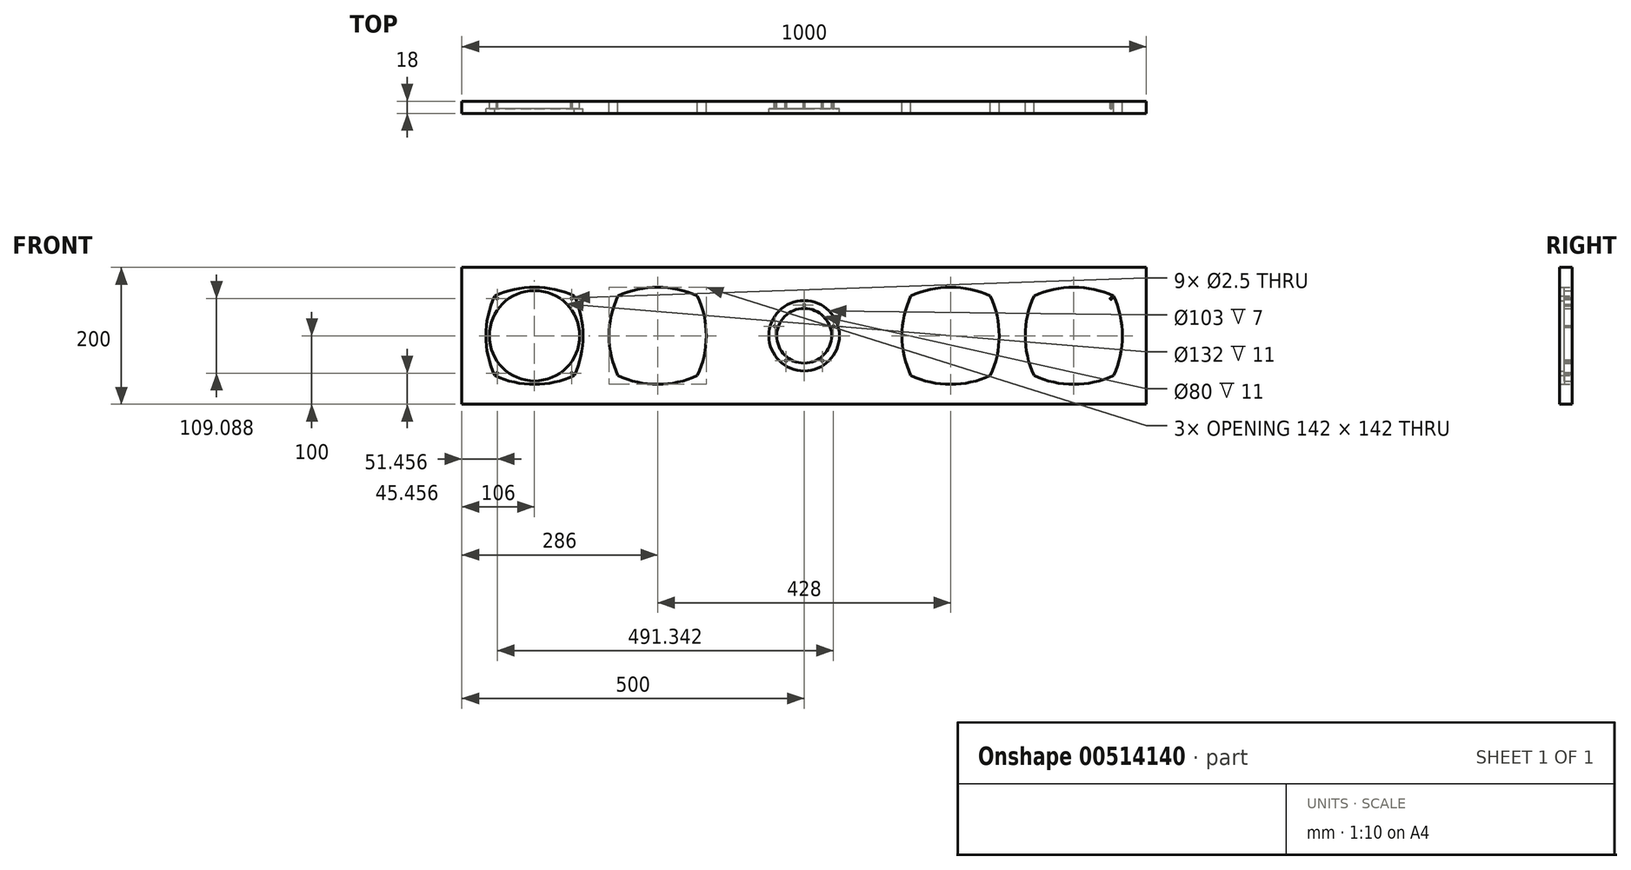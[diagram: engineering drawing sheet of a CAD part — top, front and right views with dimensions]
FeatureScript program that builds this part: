
annotation { "Feature Type Name" : "Feature", "Feature Type Description" : "" }
export const myFeature = defineFeature(function(context is Context, id is Id, definition is map)
    precondition{}
    {
        {
            var Q0;
            Q0=qCreatedBy(makeId("Front.planeOp"),FACE);
            var sketch = newSketch(context, id + "F0", { "sketchPlane" : qUnion([Q0])});
            skLineSegment(sketch, "E0.bottom", {"start": v(500, 100) * mm, "end": v(-500, 100) * mm});
            skLineSegment(sketch, "E0.top", {"start": v(500, -100) * mm, "end": v(-500, -100) * mm});
            skLineSegment(sketch, "E0.left", {"start": v(500, 100) * mm, "end": v(500, -100) * mm});
            skLineSegment(sketch, "E0.right", {"start": v(-500, 100) * mm, "end": v(-500, -100) * mm});
            skPoint(sketch, "E0.middle", {"position": v(0, 0) * mm});
            skCircle(sketch, "E1", {"center": v(-394, 0) * mm, "radius": 66 * mm});
            skCircle(sketch, "E2", {"center": v(0, 0) * mm, "radius": 40 * mm});
            skCircle(sketch, "E3", {"center": v(0, 0) * mm, "radius": 45 * mm});
            skCircle(sketch, "E4", {"center": v(0, 0) * mm, "radius": 51.5 * mm});
            skCircle(sketch, "E5", {"center": v(0, 45) * mm, "radius": 1.25 * mm});
            skCircle(sketch, "E6.1.0", {"center": v(-42.8, 13.9) * mm, "radius": 1.25 * mm});
            skCircle(sketch, "E6.2.0", {"center": v(-26.45, -36.4) * mm, "radius": 1.25 * mm});
            skCircle(sketch, "E6.3.0", {"center": v(26.45, -36.4) * mm, "radius": 1.25 * mm});
            skCircle(sketch, "E6.4.0", {"center": v(42.8, 13.9) * mm, "radius": 1.25 * mm});
            skArc(sketch, "E7", {"start": v(-335.92, 58.08) * mm, "mid": v(-394, 71) * mm, "end": v(-452.08, 58.08) * mm});
            skArc(sketch, "E8", {"start": v(-452.08, 58.08) * mm, "mid": v(-465, 0) * mm, "end": v(-452.08, -58.08) * mm});
            skArc(sketch, "E9", {"start": v(-452.08, -58.08) * mm, "mid": v(-394, -71) * mm, "end": v(-335.92, -58.08) * mm});
            skArc(sketch, "E10", {"start": v(-335.92, -58.08) * mm, "mid": v(-323, 0) * mm, "end": v(-335.92, 58.08) * mm});
            skLineSegment(sketch, "E11", {"start": v(-452.08, 58.08) * mm, "end": v(-335.92, -58.08) * mm, "construction": true});
            skLineSegment(sketch, "E12", {"start": v(-335.92, 58.08) * mm, "end": v(-452.08, -58.08) * mm, "construction": true});
            skCircle(sketch, "E13", {"center": v(-448.54, 54.54) * mm, "radius": 1.25 * mm});
            skCircle(sketch, "E14.1.0", {"center": v(-448.54, -54.54) * mm, "radius": 1.25 * mm});
            skCircle(sketch, "E14.2.0", {"center": v(-339.46, -54.54) * mm, "radius": 1.25 * mm});
            skCircle(sketch, "E14.3.0", {"center": v(-339.46, 54.54) * mm, "radius": 1.25 * mm});
            skCircle(sketch, "E15.MirrorC", {"center": v(448.54, 54.54) * mm, "radius": 1.25 * mm});
            skCircle(sketch, "E16.MirrorC", {"center": v(339.46, -54.54) * mm, "radius": 1.25 * mm});
            skCircle(sketch, "E17.MirrorC", {"center": v(448.54, -54.54) * mm, "radius": 1.25 * mm});
            skCircle(sketch, "E18.MirrorC", {"center": v(339.46, 54.54) * mm, "radius": 1.25 * mm});
            skLineSegment(sketch, "E19.MirrorCS", {"start": v(335.92, 58.08) * mm, "end": v(452.08, -58.08) * mm, "construction": true});
            skLineSegment(sketch, "E20.MirrorCS", {"start": v(452.08, 58.08) * mm, "end": v(335.92, -58.08) * mm, "construction": true});
            skPoint(sketch, "E21.MirrorP", {"position": v(394, 0) * mm});
            skArc(sketch, "E22.MirrorCS", {"start": v(452.08, 58.08) * mm, "mid": v(465, 0) * mm, "end": v(452.08, -58.08) * mm});
            skArc(sketch, "E23.MirrorCS", {"start": v(452.08, -58.08) * mm, "mid": v(394, -71) * mm, "end": v(335.92, -58.08) * mm});
            skCircle(sketch, "E24.MirrorC", {"center": v(394, 0) * mm, "radius": 66 * mm});
            skArc(sketch, "E25.MirrorCS", {"start": v(335.92, -58.08) * mm, "mid": v(323, 0) * mm, "end": v(335.92, 58.08) * mm});
            skArc(sketch, "E26.MirrorCS", {"start": v(335.92, 58.08) * mm, "mid": v(394, 71) * mm, "end": v(452.08, 58.08) * mm});
            skCircle(sketch, "E27", {"center": v(-214, 0) * mm, "radius": 66 * mm});
            skArc(sketch, "E28", {"start": v(-155.92, 58.08) * mm, "mid": v(-214, 71) * mm, "end": v(-272.08, 58.08) * mm});
            skArc(sketch, "E29", {"start": v(-272.08, 58.08) * mm, "mid": v(-285, 0) * mm, "end": v(-272.08, -58.08) * mm});
            skArc(sketch, "E30", {"start": v(-272.08, -58.08) * mm, "mid": v(-214, -71) * mm, "end": v(-155.92, -58.08) * mm});
            skArc(sketch, "E31", {"start": v(-155.92, -58.08) * mm, "mid": v(-143, 0) * mm, "end": v(-155.92, 58.08) * mm});
            skLineSegment(sketch, "E32", {"start": v(-272.08, 58.08) * mm, "end": v(-155.92, -58.08) * mm, "construction": true});
            skLineSegment(sketch, "E33", {"start": v(-155.92, 58.08) * mm, "end": v(-272.08, -58.08) * mm, "construction": true});
            skCircle(sketch, "E34", {"center": v(-268.54, 54.54) * mm, "radius": 1.25 * mm});
            skCircle(sketch, "E35.1.0", {"center": v(-268.54, -54.54) * mm, "radius": 1.25 * mm});
            skCircle(sketch, "E35.2.0", {"center": v(-159.46, -54.54) * mm, "radius": 1.25 * mm});
            skCircle(sketch, "E35.3.0", {"center": v(-159.46, 54.54) * mm, "radius": 1.25 * mm});
            skCircle(sketch, "E36.MirrorC", {"center": v(268.54, 54.54) * mm, "radius": 1.25 * mm});
            skCircle(sketch, "E37.MirrorC", {"center": v(268.54, -54.54) * mm, "radius": 1.25 * mm});
            skCircle(sketch, "E38.MirrorC", {"center": v(159.46, -54.54) * mm, "radius": 1.25 * mm});
            skCircle(sketch, "E39.MirrorC", {"center": v(159.46, 54.54) * mm, "radius": 1.25 * mm});
            skArc(sketch, "E40.MirrorCS", {"start": v(155.92, 58.08) * mm, "mid": v(214, 71) * mm, "end": v(272.08, 58.08) * mm});
            skLineSegment(sketch, "E41.MirrorCS", {"start": v(272.08, 58.08) * mm, "end": v(155.92, -58.08) * mm, "construction": true});
            skLineSegment(sketch, "E42.MirrorCS", {"start": v(155.92, 58.08) * mm, "end": v(272.08, -58.08) * mm, "construction": true});
            skArc(sketch, "E43.MirrorCS", {"start": v(155.92, -58.08) * mm, "mid": v(143, 0) * mm, "end": v(155.92, 58.08) * mm});
            skArc(sketch, "E44.MirrorCS", {"start": v(272.08, -58.08) * mm, "mid": v(214, -71) * mm, "end": v(155.92, -58.08) * mm});
            skPoint(sketch, "E45.MirrorP", {"position": v(214, 0) * mm});
            skCircle(sketch, "E46.MirrorC", {"center": v(214, 0) * mm, "radius": 66 * mm});
            skArc(sketch, "E47.MirrorCS", {"start": v(272.08, 58.08) * mm, "mid": v(285, 0) * mm, "end": v(272.08, -58.08) * mm});
            skSolve(sketch);
        }
        {
            var Q0;
            {var subQ0=sQuery(id+"F0.wireOp",EDGE,"OdRPwVkJ-LgnD-wcSP-26Xd-tCm6PIhxOoPI.bottom");var subQ1=sQuery(id+"F0.wireOp",EDGE,"WheFQNC1-m6lz-ETYG-WdT4-gUt766dIlw9O");var subQ2=makeQuery(id+"F0.imprint","INTERSECT",VERTEX,{"disambiguationData":[OD(0.0)],"derivedFrom":[subQ1,subQ0]});Q0=makeQuery(id+"F0.imprint","IMPRINT",FACE,{"disambiguationData":[TD([[makeQuery(id+"F0.imprint","IMPRINT",EDGE,{"disambiguationData":[TD([[subQ2,-1.0]])],"derivedFrom":subQ1}),1.0]])]});}
            var Q1;
            {var subQ0=sQuery(id+"F0.wireOp",EDGE,"OdRPwVkJ-LgnD-wcSP-26Xd-tCm6PIhxOoPI.bottom");var subQ1=sQuery(id+"F0.wireOp",EDGE,"WheFQNC1-m6lz-ETYG-WdT4-gUt766dIlw9O");var subQ2=makeQuery(id+"F0.imprint","INTERSECT",VERTEX,{"disambiguationData":[OD(0.0)],"derivedFrom":[subQ1,subQ0]});Q1=makeQuery(id+"F0.imprint","IMPRINT",FACE,{"disambiguationData":[TD([[makeQuery(id+"F0.imprint","IMPRINT",EDGE,{"disambiguationData":[TD([[subQ2,1.0]])],"derivedFrom":subQ1}),-1.0]])]});}
            var Q2;
            {var subQ0=sQuery(id+"F0.wireOp",EDGE,"OdRPwVkJ-LgnD-wcSP-26Xd-tCm6PIhxOoPI.bottom");var subQ1=sQuery(id+"F0.wireOp",EDGE,"WheFQNC1-m6lz-ETYG-WdT4-gUt766dIlw9O");var subQ2=makeQuery(id+"F0.imprint","INTERSECT",VERTEX,{"disambiguationData":[OD(1.0)],"derivedFrom":[subQ1,subQ0]});Q2=makeQuery(id+"F0.imprint","IMPRINT",FACE,{"disambiguationData":[TD([[makeQuery(id+"F0.imprint","IMPRINT",EDGE,{"disambiguationData":[TD([[subQ2,-1.0]])],"derivedFrom":subQ1}),-1.0]])]});}
            var Q3;
            {var subQ0=sQuery(id+"F0.wireOp",EDGE,"OdRPwVkJ-LgnD-wcSP-26Xd-tCm6PIhxOoPI.right");var subQ1=sQuery(id+"F0.wireOp",EDGE,"WheFQNC1-m6lz-ETYG-WdT4-gUt766dIlw9O");var subQ2=makeQuery(id+"F0.imprint","INTERSECT",VERTEX,{"disambiguationData":[OD(0.0)],"derivedFrom":[subQ1,subQ0]});Q3=makeQuery(id+"F0.imprint","IMPRINT",FACE,{"disambiguationData":[TD([[makeQuery(id+"F0.imprint","IMPRINT",EDGE,{"disambiguationData":[TD([[subQ2,-1.0]])],"derivedFrom":subQ1}),1.0]])]});}
            var Q4;
            {var subQ0=sQuery(id+"F0.wireOp",EDGE,"OdRPwVkJ-LgnD-wcSP-26Xd-tCm6PIhxOoPI.top");var subQ1=sQuery(id+"F0.wireOp",EDGE,"WheFQNC1-m6lz-ETYG-WdT4-gUt766dIlw9O");var subQ2=makeQuery(id+"F0.imprint","INTERSECT",VERTEX,{"disambiguationData":[OD(0.0)],"derivedFrom":[subQ1,subQ0]});Q4=makeQuery(id+"F0.imprint","IMPRINT",FACE,{"disambiguationData":[TD([[makeQuery(id+"F0.imprint","IMPRINT",EDGE,{"disambiguationData":[TD([[subQ2,-1.0]])],"derivedFrom":subQ1}),1.0]])]});}
            var Q5;
            {var subQ0=sQuery(id+"F0.wireOp",EDGE,"OdRPwVkJ-LgnD-wcSP-26Xd-tCm6PIhxOoPI.right");var subQ1=sQuery(id+"F0.wireOp",EDGE,"WheFQNC1-m6lz-ETYG-WdT4-gUt766dIlw9O");var subQ2=makeQuery(id+"F0.imprint","INTERSECT",VERTEX,{"disambiguationData":[OD(1.0)],"derivedFrom":[subQ1,subQ0]});Q5=makeQuery(id+"F0.imprint","IMPRINT",FACE,{"disambiguationData":[TD([[makeQuery(id+"F0.imprint","IMPRINT",EDGE,{"disambiguationData":[TD([[subQ2,-1.0]])],"derivedFrom":subQ1}),-1.0]])]});}
            var Q6;
            {var subQ0=sQuery(id+"F0.wireOp",EDGE,"OdRPwVkJ-LgnD-wcSP-26Xd-tCm6PIhxOoPI.top");var subQ1=sQuery(id+"F0.wireOp",EDGE,"WheFQNC1-m6lz-ETYG-WdT4-gUt766dIlw9O");var subQ2=makeQuery(id+"F0.imprint","INTERSECT",VERTEX,{"disambiguationData":[OD(1.0)],"derivedFrom":[subQ1,subQ0]});Q6=makeQuery(id+"F0.imprint","IMPRINT",FACE,{"disambiguationData":[TD([[makeQuery(id+"F0.imprint","IMPRINT",EDGE,{"disambiguationData":[TD([[subQ2,-1.0]])],"derivedFrom":subQ1}),-1.0]])]});}
            var Q7;
            {var subQ0=sQuery(id+"F0.wireOp",EDGE,"OdRPwVkJ-LgnD-wcSP-26Xd-tCm6PIhxOoPI.left");var subQ1=sQuery(id+"F0.wireOp",EDGE,"WheFQNC1-m6lz-ETYG-WdT4-gUt766dIlw9O");var subQ2=makeQuery(id+"F0.imprint","INTERSECT",VERTEX,{"disambiguationData":[OD(0.0)],"derivedFrom":[subQ1,subQ0]});Q7=makeQuery(id+"F0.imprint","IMPRINT",FACE,{"disambiguationData":[TD([[makeQuery(id+"F0.imprint","IMPRINT",EDGE,{"disambiguationData":[TD([[subQ2,1.0]])],"derivedFrom":subQ1}),1.0]])]});}
            var Q8;
            {var subQ0=sQuery(id+"F0.wireOp",EDGE,"E167.MirrorCS");var subQ1=sQuery(id+"F0.wireOp",EDGE,"E162.MirrorC");var subQ2=makeQuery(id+"F0.imprint","INTERSECT",VERTEX,{"disambiguationData":[OD(0.0)],"derivedFrom":[subQ1,subQ0]});Q8=makeQuery(id+"F0.imprint","IMPRINT",FACE,{"disambiguationData":[TD([[makeQuery(id+"F0.imprint","IMPRINT",EDGE,{"disambiguationData":[TD([[subQ2,-1.0]])],"derivedFrom":subQ1}),-1.0]])]});}
            var Q9;
            {var subQ0=sQuery(id+"F0.wireOp",EDGE,"E167.MirrorCS");var subQ1=sQuery(id+"F0.wireOp",EDGE,"E162.MirrorC");var subQ2=makeQuery(id+"F0.imprint","INTERSECT",VERTEX,{"disambiguationData":[OD(0.0)],"derivedFrom":[subQ1,subQ0]});Q9=makeQuery(id+"F0.imprint","IMPRINT",FACE,{"disambiguationData":[TD([[makeQuery(id+"F0.imprint","IMPRINT",EDGE,{"disambiguationData":[TD([[subQ2,1.0]])],"derivedFrom":subQ1}),1.0]])]});}
            var Q10;
            {var subQ0=sQuery(id+"F0.wireOp",EDGE,"E164.MirrorCS");var subQ1=sQuery(id+"F0.wireOp",EDGE,"E162.MirrorC");var subQ2=makeQuery(id+"F0.imprint","INTERSECT",VERTEX,{"disambiguationData":[OD(1.0)],"derivedFrom":[subQ1,subQ0]});Q10=makeQuery(id+"F0.imprint","IMPRINT",FACE,{"disambiguationData":[TD([[makeQuery(id+"F0.imprint","IMPRINT",EDGE,{"disambiguationData":[TD([[subQ2,-1.0]])],"derivedFrom":subQ1}),1.0]])]});}
            var Q11;
            {var subQ0=sQuery(id+"F0.wireOp",EDGE,"E168.MirrorCS");var subQ1=sQuery(id+"F0.wireOp",EDGE,"E162.MirrorC");var subQ2=makeQuery(id+"F0.imprint","INTERSECT",VERTEX,{"disambiguationData":[OD(0.0)],"derivedFrom":[subQ1,subQ0]});Q11=makeQuery(id+"F0.imprint","IMPRINT",FACE,{"disambiguationData":[TD([[makeQuery(id+"F0.imprint","IMPRINT",EDGE,{"disambiguationData":[TD([[subQ2,1.0]])],"derivedFrom":subQ1}),-1.0]])]});}
            var Q12;
            {var subQ0=sQuery(id+"F0.wireOp",EDGE,"E167.MirrorCS");var subQ1=sQuery(id+"F0.wireOp",EDGE,"E162.MirrorC");var subQ2=makeQuery(id+"F0.imprint","INTERSECT",VERTEX,{"disambiguationData":[OD(1.0)],"derivedFrom":[subQ1,subQ0]});Q12=makeQuery(id+"F0.imprint","IMPRINT",FACE,{"disambiguationData":[TD([[makeQuery(id+"F0.imprint","IMPRINT",EDGE,{"disambiguationData":[TD([[subQ2,-1.0]])],"derivedFrom":subQ1}),1.0]])]});}
            var Q13;
            {var subQ0=sQuery(id+"F0.wireOp",EDGE,"E165.MirrorCS");var subQ1=sQuery(id+"F0.wireOp",EDGE,"E162.MirrorC");var subQ2=makeQuery(id+"F0.imprint","INTERSECT",VERTEX,{"disambiguationData":[OD(0.0)],"derivedFrom":[subQ1,subQ0]});Q13=makeQuery(id+"F0.imprint","IMPRINT",FACE,{"disambiguationData":[TD([[makeQuery(id+"F0.imprint","IMPRINT",EDGE,{"disambiguationData":[TD([[subQ2,-1.0]])],"derivedFrom":subQ1}),-1.0]])]});}
            var Q14;
            {var subQ0=sQuery(id+"F0.wireOp",EDGE,"E165.MirrorCS");var subQ1=sQuery(id+"F0.wireOp",EDGE,"E162.MirrorC");var subQ2=makeQuery(id+"F0.imprint","INTERSECT",VERTEX,{"disambiguationData":[OD(1.0)],"derivedFrom":[subQ1,subQ0]});Q14=makeQuery(id+"F0.imprint","IMPRINT",FACE,{"disambiguationData":[TD([[makeQuery(id+"F0.imprint","IMPRINT",EDGE,{"disambiguationData":[TD([[subQ2,-1.0]])],"derivedFrom":subQ1}),1.0]])]});}
            var Q15;
            {var subQ0=sQuery(id+"F0.wireOp",EDGE,"E164.MirrorCS");var subQ1=sQuery(id+"F0.wireOp",EDGE,"E162.MirrorC");var subQ2=makeQuery(id+"F0.imprint","INTERSECT",VERTEX,{"disambiguationData":[OD(0.0)],"derivedFrom":[subQ1,subQ0]});Q15=makeQuery(id+"F0.imprint","IMPRINT",FACE,{"disambiguationData":[TD([[makeQuery(id+"F0.imprint","IMPRINT",EDGE,{"disambiguationData":[TD([[subQ2,-1.0]])],"derivedFrom":subQ1}),-1.0]])]});}
            var Q16;
            Q16=makeQuery(id+"F0.imprint","IMPRINT",FACE,{"disambiguationData":[TD([[makeQuery(id+"F0.imprint","IMPRINT",EDGE,{"derivedFrom":sQuery(id+"F0.wireOp",EDGE,"E0.bottom")}),1.0]])]});
            extrude(context, id + "F1", {"entities" : qUnion([Q0, Q1, Q2, Q3, Q4, Q5, Q6, Q7, Q8, Q9, Q10, Q11, Q12, Q13, Q14, Q15, Q16]), "depth" : 18 * mm, "offsetDistance" : 25 * mm});
        }
        {
            var Q0;
            Q0=makeQuery(id+"F0.imprint","IMPRINT",FACE,{"disambiguationData":[TD([[makeQuery(id+"F0.imprint","IMPRINT",EDGE,{"derivedFrom":sQuery(id+"F0.wireOp",EDGE,"E1")}),-1.0]])]});
            var Q1;
            Q1=makeQuery(id+"F0.imprint","IMPRINT",FACE,{"disambiguationData":[TD([[makeQuery(id+"F0.imprint","IMPRINT",EDGE,{"derivedFrom":sQuery(id+"F0.wireOp",EDGE,"gHoM9Zjh-UyZu-LIRP-T4ZT-wTLvykPbdl1G")}),-1.0]])]});
            var Q2;
            Q2=makeQuery(id+"F0.imprint","IMPRINT",FACE,{"disambiguationData":[TD([[makeQuery(id+"F0.imprint","IMPRINT",EDGE,{"derivedFrom":sQuery(id+"F0.wireOp",EDGE,"a2a51c21-18e9-4a58-a1b0-e3e05ef108d85.MirrorC")}),1.0]])]});
            var Q3;
            Q3=makeQuery(id+"F0.imprint","IMPRINT",FACE,{"disambiguationData":[TD([[makeQuery(id+"F0.imprint","IMPRINT",EDGE,{"derivedFrom":sQuery(id+"F0.wireOp",EDGE,"E15.MirrorC")}),1.0]])]});
            var Q4;
            Q4=makeQuery(id+"F0.imprint","IMPRINT",FACE,{"disambiguationData":[TD([[makeQuery(id+"F0.imprint","IMPRINT",EDGE,{"derivedFrom":sQuery(id+"F0.wireOp",EDGE,"E4")}),1.0]])]});
            var Q5;
            Q5=makeQuery(id+"F0.imprint","IMPRINT",FACE,{"disambiguationData":[TD([[makeQuery(id+"F0.imprint","IMPRINT",EDGE,{"derivedFrom":sQuery(id+"F0.wireOp",EDGE,"E2")}),-1.0]])]});
            extrude(context, id + "F2", {"entities" : qUnion([Q0, Q1, Q2, Q3, Q4, Q5]), "operationType" : NewBodyOperationType.ADD, "depth" : 11 * mm, "offsetDistance" : 25 * mm});
        }
    });
